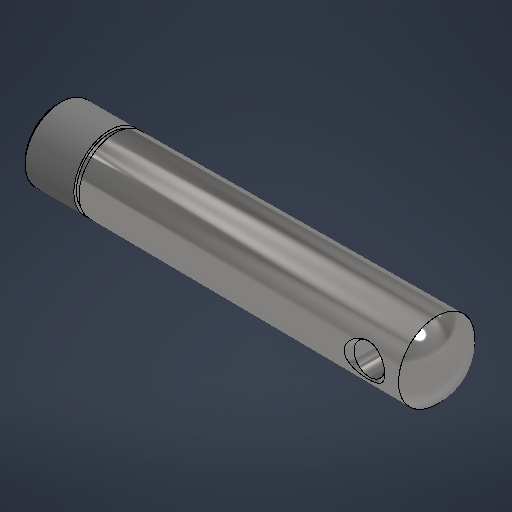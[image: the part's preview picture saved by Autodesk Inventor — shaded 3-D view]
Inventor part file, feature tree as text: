
AUTODESK INVENTOR PART (.ipt)
format: ipt  version: 2025.3 (Build 293356000, 356)  size: 302,592 bytes
history: native  units: mm
features: sketch x3, revolve x2, hole x1, extrude x1, mirror x1, chamfer x1
ambient origin geometry x8: Origin, YZ Plane, XZ Plane, XY Plane, X Axis, Y Axis, Z Axis, Center Point
bodies: Solid1 (feature_tree)
feature tree (9):
  sketch  "Sketch1"  dims[d4=0.066323mm d5=10.2mm]
  revolve  "Revolution1"  [1 undecoded]
  hole  "Hole1"  [1 undecoded]
  extrude  "Extrusion1"  TaperAngle=60.0deg  [1 undecoded]
  revolve  "Revolution2"  [1 undecoded]
  mirror  "Mirror1"
  chamfer  "Chamfer1"  Distance=77.0mm
  sketch  "Sketch2"  dims[d6=14.0mm d7=14.0mm]
  sketch  "Sketch3"  dims[d11=50.0mm d13=60.0deg d19=10.0mm d20=77.0mm d21=67.0mm d22=6.0mm d23=0.5mm d24=10.0mm d25=1.0mm d26=360.0deg d27=0.0mm d28=0.0mm d29=45.0deg d30=1.0mm d31=90.0deg d32=14.83181mm d35=10.106mm d36=35.0mm d37=4.0mm d38=2.0mm d39=90.0deg d40=50.0mm d41=120.0deg d42=0.5mm d43=2.0mm d44=45.0deg]
note: 4 required parameter values undecoded (feature->parameter linkage not recoverable at this tier; creation-order binding heuristic only, values carry confidence <= 0.55)